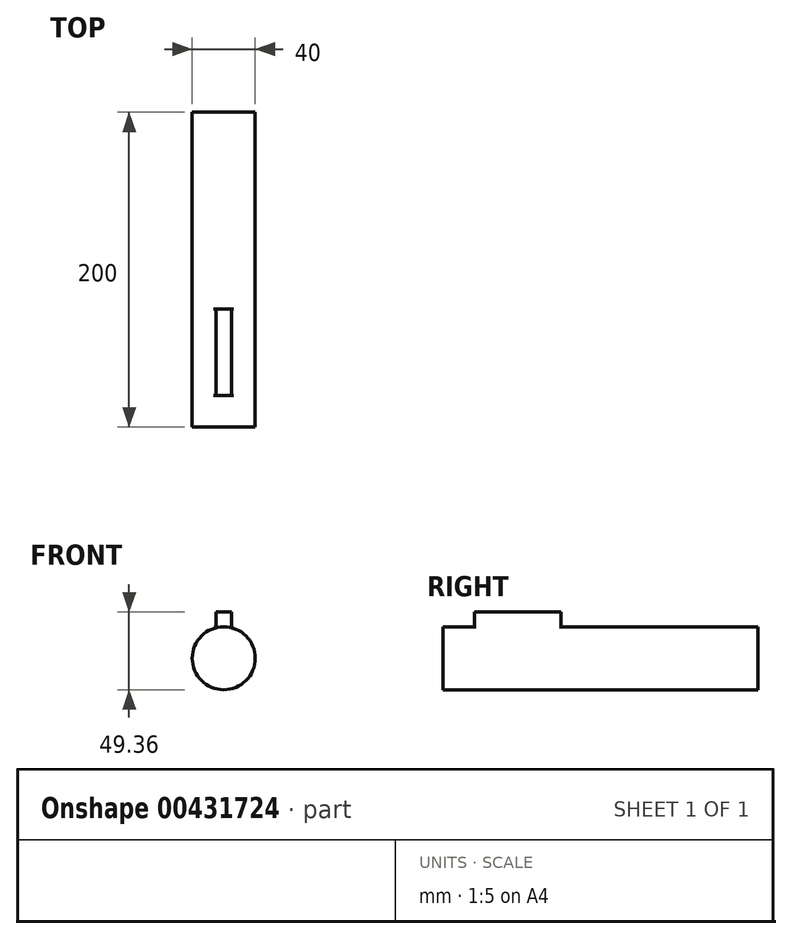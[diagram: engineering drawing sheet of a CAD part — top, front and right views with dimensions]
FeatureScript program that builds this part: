
annotation { "Feature Type Name" : "Feature", "Feature Type Description" : "" }
export const myFeature = defineFeature(function(context is Context, id is Id, definition is map)
    precondition{}
    {
        {
            var Q0;
            Q0=qCreatedBy(makeId("Front.planeOp"),FACE);
            var sketch = newSketch(context, id + "F0", { "sketchPlane" : qUnion([Q0])});
            skCircle(sketch, "E0", {"center": v(0, 0) * mm, "radius": 20 * mm});
            skSolve(sketch);
        }
        {
            var Q0;
            Q0 = qSketchRegion(id + "F0", true);
            extrude(context, id + "F1", {"entities" : qUnion([Q0]), "oppositeDirection" : true, "depth" : 20 * mm});
        }
        {
            var Q0;
            Q0=makeQuery(id+"F1.opExtrude","CAP_FACE",FACE,{"disambiguationData":[OSD([sQuery(id+"F0.wireOp",EDGE,"E0")])],"isStart":false});
            var sketch = newSketch(context, id + "F2", { "sketchPlane" : qUnion([Q0])});
            skArc(sketch, "E1", {"start": v(-6.36, 18.96) * mm, "mid": v(0, -20) * mm, "end": v(6.36, 18.96) * mm});
            skLineSegment(sketch, "E2", {"start": v(-5, 20.86) * mm, "end": v(-5, 29.36) * mm});
            skLineSegment(sketch, "E3", {"start": v(-5, 29.36) * mm, "end": v(5, 29.36) * mm});
            skLineSegment(sketch, "E4", {"start": v(5, 29.36) * mm, "end": v(5, 20.86) * mm});
            skLineSegment(sketch, "E5", {"start": v(0, 0) * mm, "end": v(0, 54.94) * mm, "construction": true});
            skPoint(sketch, "E6", {"position": v(0, 29.36) * mm});
            skPoint(sketch, "E7.visualSharp", {"position": v(5, 19.36) * mm});
            skArc(sketch, "E7.filletArc", {"start": v(5, 20.86) * mm, "mid": v(5.38, 19.69) * mm, "end": v(6.36, 18.96) * mm});
            skPoint(sketch, "E8.visualSharp", {"position": v(-5, 19.36) * mm});
            skArc(sketch, "E8.filletArc", {"start": v(-6.36, 18.96) * mm, "mid": v(-5.38, 19.69) * mm, "end": v(-5, 20.86) * mm});
            skSolve(sketch);
        }
        {
            var Q0;
            {var subQ0=sQuery(id+"F2.wireOp",EDGE,"E1");Q0=makeQuery(id+"F2.imprint","IMPRINT",FACE,{"disambiguationData":[TD([[makeQuery(id+"F2.imprint","IMPRINT",EDGE,{"derivedFrom":subQ0}),-1.0]])]});}
            var Q1;
            Q1=makeQuery(id+"F2.imprint","IMPRINT",FACE,{"disambiguationData":[TD([[makeQuery(id+"F2.imprint","IMPRINT",EDGE,{"derivedFrom":sQuery(id+"F2.wireOp",EDGE,"E2")}),-1.0]])]});
            var Q2;
            Q2=makeQuery(id+"F1.opExtrude","CAP_FACE",FACE,{"disambiguationData":[OSD([sQuery(id+"F0.wireOp",EDGE,"E0")])],"isStart":true});
            extrude(context, id + "F3", {"entities" : qUnion([Q0, Q1, Q2]), "operationType" : NewBodyOperationType.ADD, "depth" : 55 * mm});
        }
        {
            var Q0;
            Q0=makeQuery(id+"F3.opExtrude","CAP_FACE",FACE,{"disambiguationData":[OSD([sQuery(id+"F2.wireOp",EDGE,"E1"),sQuery(id+"F2.wireOp",EDGE,"E2"),sQuery(id+"F2.wireOp",EDGE,"E3"),sQuery(id+"F2.wireOp",EDGE,"E4"),sQuery(id+"F2.wireOp",EDGE,"E7.filletArc"),sQuery(id+"F2.wireOp",EDGE,"E8.filletArc")])],"isStart":false});
            var sketch = newSketch(context, id + "F4", { "sketchPlane" : qUnion([Q0])});
            skCircle(sketch, "E9", {"center": v(0, 0) * mm, "radius": 20 * mm});
            skSolve(sketch);
        }
        {
            var Q0;
            Q0 = qSketchRegion(id + "F4", true);
            extrude(context, id + "F5", {"entities" : qUnion([Q0]), "operationType" : NewBodyOperationType.ADD, "depth" : 125 * mm});
        }
    });
